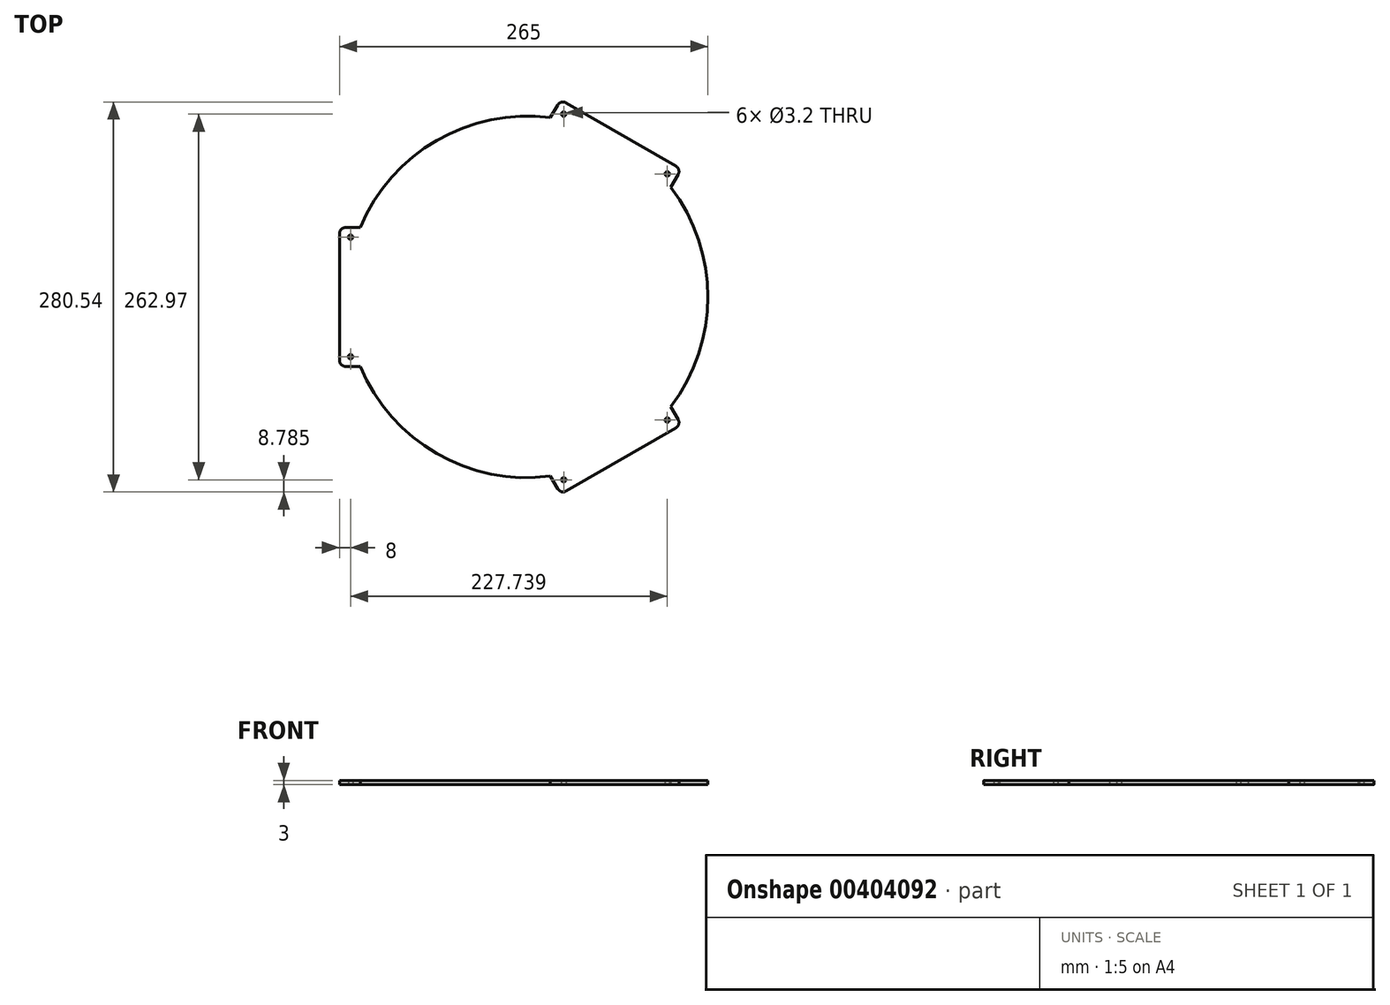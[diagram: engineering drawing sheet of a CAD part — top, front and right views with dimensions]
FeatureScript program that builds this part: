
annotation { "Feature Type Name" : "Feature", "Feature Type Description" : "" }
export const myFeature = defineFeature(function(context is Context, id is Id, definition is map)
    precondition{}
    {
        {
            var Q0;
            Q0=qCreatedBy(makeId("Top.planeOp"),FACE);
            var sketch = newSketch(context, id + "F0", { "sketchPlane" : qUnion([Q0])});
            skCircle(sketch, "E0", {"center": v(0, 0) * mm, "radius": 130 * mm});
            skLineSegment(sketch, "E1.bottom", {"start": v(-130.5, 50) * mm, "end": v(-120, 50) * mm});
            skLineSegment(sketch, "E1.top", {"start": v(-130.5, -50) * mm, "end": v(-120, -50) * mm});
            skLineSegment(sketch, "E1.left", {"start": v(-135, 45.5) * mm, "end": v(-135, -45.5) * mm});
            skLineSegment(sketch, "E1.right", {"start": v(-120, 50) * mm, "end": v(-120, -50) * mm});
            skPoint(sketch, "E2", {"position": v(-127, 43) * mm});
            skPoint(sketch, "E3.visualSharp", {"position": v(-135, 50) * mm});
            skArc(sketch, "E3.filletArc", {"start": v(-130.5, 50) * mm, "mid": v(-133.68, 48.68) * mm, "end": v(-135, 45.5) * mm});
            skPoint(sketch, "E4.visualSharp", {"position": v(-135, -50) * mm});
            skArc(sketch, "E4.filletArc", {"start": v(-135, -45.5) * mm, "mid": v(-133.68, -48.68) * mm, "end": v(-130.5, -50) * mm});
            skLineSegment(sketch, "E5.bottom", {"start": v(28.1, 139.66) * mm, "end": v(106.9, 94.16) * mm});
            skLineSegment(sketch, "E5.top", {"start": v(16.7, 128.92) * mm, "end": v(103.3, 78.92) * mm});
            skLineSegment(sketch, "E5.left", {"start": v(21.95, 138.02) * mm, "end": v(16.7, 128.92) * mm});
            skLineSegment(sketch, "E5.right", {"start": v(108.55, 88.02) * mm, "end": v(103.3, 78.92) * mm});
            skLineSegment(sketch, "E6.bottom", {"start": v(108.55, -88.02) * mm, "end": v(103.3, -78.92) * mm});
            skLineSegment(sketch, "E6.top", {"start": v(21.95, -138.02) * mm, "end": v(16.7, -128.92) * mm});
            skLineSegment(sketch, "E6.left", {"start": v(106.9, -94.16) * mm, "end": v(28.1, -139.66) * mm});
            skLineSegment(sketch, "E6.right", {"start": v(103.3, -78.92) * mm, "end": v(16.7, -128.92) * mm});
            skPoint(sketch, "E7", {"position": v(26.26, -131.49) * mm});
            skPoint(sketch, "E8", {"position": v(100.74, -88.49) * mm});
            skPoint(sketch, "E9.visualSharp", {"position": v(24.2, -141.91) * mm});
            skArc(sketch, "E9.filletArc", {"start": v(21.95, -138.02) * mm, "mid": v(24.68, -140.11) * mm, "end": v(28.1, -139.66) * mm});
            skPoint(sketch, "E10.visualSharp", {"position": v(110.8, -91.91) * mm});
            skArc(sketch, "E10.filletArc", {"start": v(106.9, -94.16) * mm, "mid": v(109, -91.43) * mm, "end": v(108.55, -88.02) * mm});
            skPoint(sketch, "E11", {"position": v(26.26, 131.49) * mm});
            skPoint(sketch, "E12", {"position": v(100.74, 88.49) * mm});
            skPoint(sketch, "E13.visualSharp", {"position": v(24.2, 141.91) * mm});
            skArc(sketch, "E13.filletArc", {"start": v(28.1, 139.66) * mm, "mid": v(24.68, 140.11) * mm, "end": v(21.95, 138.02) * mm});
            skPoint(sketch, "E14.visualSharp", {"position": v(110.8, 91.91) * mm});
            skArc(sketch, "E14.filletArc", {"start": v(108.55, 88.02) * mm, "mid": v(109, 91.43) * mm, "end": v(106.9, 94.16) * mm});
            skCircle(sketch, "E15", {"center": v(-127, -43) * mm, "radius": 1.6 * mm});
            skCircle(sketch, "E16", {"center": v(-127, 43) * mm, "radius": 1.6 * mm});
            skCircle(sketch, "E17", {"center": v(26.26, 131.49) * mm, "radius": 1.6 * mm});
            skCircle(sketch, "E18", {"center": v(100.74, 88.49) * mm, "radius": 1.6 * mm});
            skCircle(sketch, "E19", {"center": v(100.74, -88.49) * mm, "radius": 1.6 * mm});
            skCircle(sketch, "E20", {"center": v(26.26, -131.49) * mm, "radius": 1.6 * mm});
            skSolve(sketch);
        }
        {
            var Q0;
            Q0=qSketchRegion(id+"F0",true);
            extrude(context, id + "F1", {"entities" : qUnion([Q0]), "depth" : 3 * mm});
        }
    });
